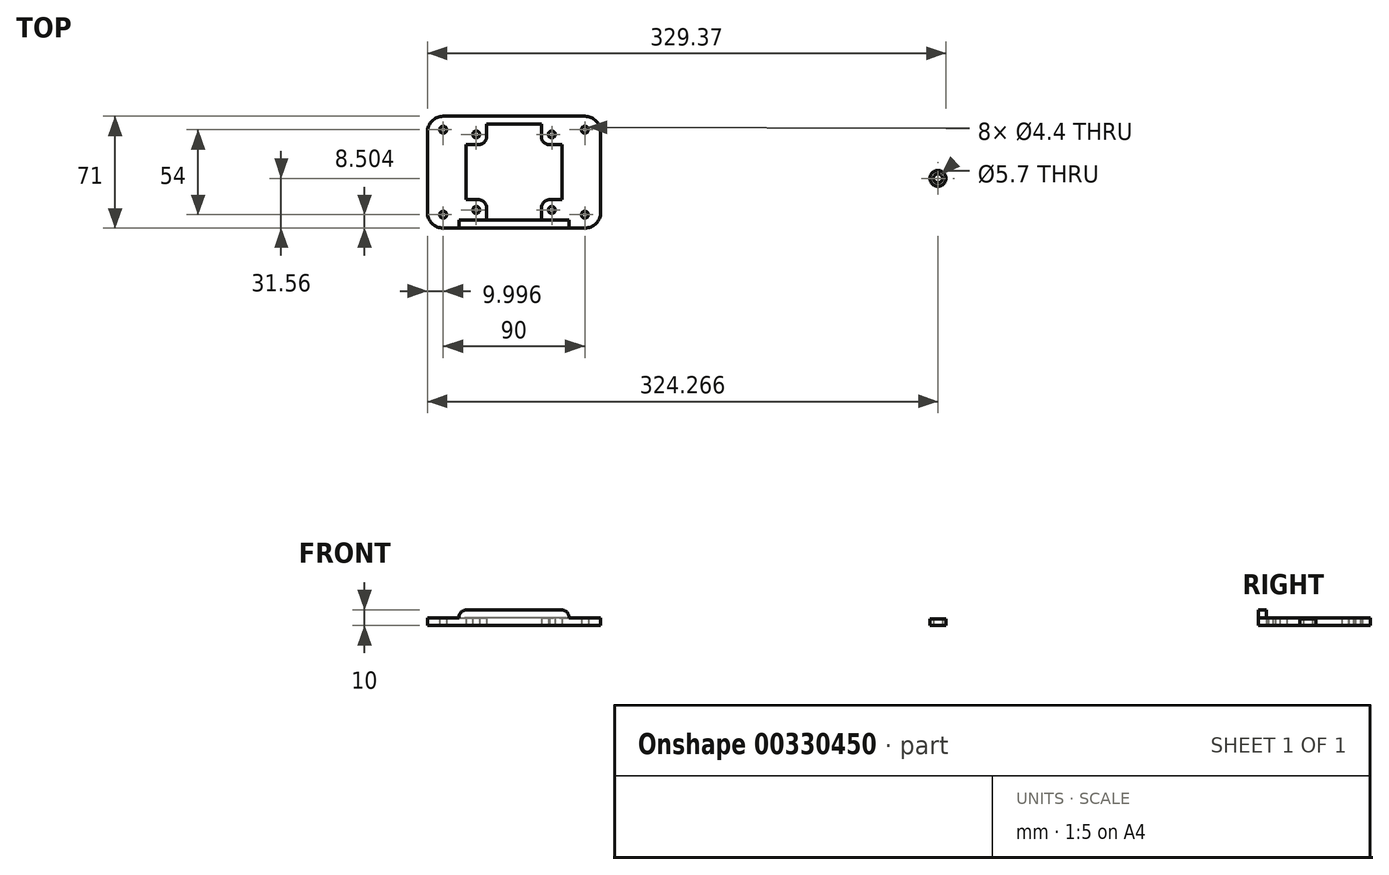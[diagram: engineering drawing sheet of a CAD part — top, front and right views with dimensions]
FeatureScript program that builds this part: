
annotation { "Feature Type Name" : "Feature", "Feature Type Description" : "" }
export const myFeature = defineFeature(function(context is Context, id is Id, definition is map)
    precondition{}
    {
        {
            var Q0;
            Q0=qCreatedBy(makeId("Top.planeOp"),FACE);
            var sketch = newSketch(context, id + "F0", { "sketchPlane" : qUnion([Q0])});
            skCircle(sketch, "E0", {"center": v(-176.65, -20.06) * mm, "radius": 2.2 * mm});
            skCircle(sketch, "E1.MirrorC", {"center": v(-128.65, -20.06) * mm, "radius": 2.2 * mm});
            skCircle(sketch, "E2.MirrorC", {"center": v(-176.65, 27.94) * mm, "radius": 2.2 * mm});
            skCircle(sketch, "E3.MirrorC", {"center": v(-128.65, 27.94) * mm, "radius": 2.2 * mm});
            skLineSegment(sketch, "E4.0", {"start": v(-183.15, -13.56) * mm, "end": v(-183.15, 21.44) * mm});
            skLineSegment(sketch, "E4.1", {"start": v(-183.15, -13.56) * mm, "end": v(-175.15, -13.56) * mm});
            skArc(sketch, "E4.2", {"start": v(-170.15, -18.56) * mm, "mid": v(-171.62, -15.02) * mm, "end": v(-175.15, -13.56) * mm});
            skLineSegment(sketch, "E4.3", {"start": v(-170.15, -26.56) * mm, "end": v(-170.15, -18.56) * mm});
            skLineSegment(sketch, "E4.4", {"start": v(-135.15, -26.56) * mm, "end": v(-170.15, -26.56) * mm});
            skLineSegment(sketch, "E4.5", {"start": v(-135.15, 34.44) * mm, "end": v(-135.15, 25.44) * mm});
            skLineSegment(sketch, "E4.6", {"start": v(-135.15, 34.44) * mm, "end": v(-170.15, 34.44) * mm});
            skLineSegment(sketch, "E4.7", {"start": v(-170.15, 34.44) * mm, "end": v(-170.15, 26.44) * mm});
            skArc(sketch, "E4.8", {"start": v(-170.15, 26.44) * mm, "mid": v(-171.62, 22.9) * mm, "end": v(-175.15, 21.44) * mm});
            skArc(sketch, "E4.9", {"start": v(-135.15, 25.44) * mm, "mid": v(-133.38, 22.54) * mm, "end": v(-130.15, 21.44) * mm});
            skLineSegment(sketch, "E4.10", {"start": v(-122.15, 21.44) * mm, "end": v(-130.15, 21.44) * mm});
            skLineSegment(sketch, "E4.11", {"start": v(-122.15, -13.56) * mm, "end": v(-122.15, 21.44) * mm});
            skLineSegment(sketch, "E4.12", {"start": v(-122.15, -13.56) * mm, "end": v(-130.15, -13.56) * mm});
            skArc(sketch, "E4.13", {"start": v(-135.15, -18.56) * mm, "mid": v(-133.69, -15.02) * mm, "end": v(-130.15, -13.56) * mm});
            skLineSegment(sketch, "E4.14", {"start": v(-183.15, 21.44) * mm, "end": v(-175.15, 21.44) * mm});
            skLineSegment(sketch, "E4.15", {"start": v(-135.15, -26.56) * mm, "end": v(-135.15, -18.56) * mm});
            skLineSegment(sketch, "E5", {"start": v(-183.15, -13.56) * mm, "end": v(-122.15, 21.44) * mm, "construction": true});
            skLineSegment(sketch, "E6", {"start": v(-152.65, 34.44) * mm, "end": v(-152.65, -26.56) * mm, "construction": true});
            skLineSegment(sketch, "E7", {"start": v(-152.65, -31.56) * mm, "end": v(-207.65, -31.56) * mm});
            skLineSegment(sketch, "E8", {"start": v(-207.65, -31.56) * mm, "end": v(-207.65, 39.44) * mm});
            skLineSegment(sketch, "E9", {"start": v(-207.65, 39.44) * mm, "end": v(-152.65, 39.44) * mm});
            skCircle(sketch, "E10", {"center": v(-197.65, 30.94) * mm, "radius": 2.2 * mm});
            skCircle(sketch, "E11", {"center": v(-197.65, -23.06) * mm, "radius": 2.2 * mm});
            skLineSegment(sketch, "E12", {"start": v(-183.15, 3.94) * mm, "end": v(-207.65, 3.94) * mm, "construction": true});
            skLineSegment(sketch, "E13.MirrorCS", {"start": v(-152.65, -31.56) * mm, "end": v(-97.65, -31.56) * mm});
            skLineSegment(sketch, "E14.MirrorCS", {"start": v(-97.65, 39.44) * mm, "end": v(-152.65, 39.44) * mm});
            skLineSegment(sketch, "E15.MirrorCS", {"start": v(-97.65, -31.56) * mm, "end": v(-97.65, 39.44) * mm});
            skCircle(sketch, "E16.MirrorC", {"center": v(-107.65, 30.94) * mm, "radius": 2.2 * mm});
            skCircle(sketch, "E17.MirrorC", {"center": v(-107.65, -23.06) * mm, "radius": 2.2 * mm});
            skSolve(sketch);
        }
        {
            var Q0;
            Q0=makeQuery(id+"F0.imprint","IMPRINT",FACE,{"disambiguationData":[TD([[makeQuery(id+"F0.imprint","IMPRINT",EDGE,{"derivedFrom":sQuery(id+"F0.wireOp",EDGE,"E0")}),-1.0]])]});
            extrude(context, id + "F1", {"entities" : qUnion([Q0]), "depth" : 5 * mm, "offsetDistance" : 25 * mm});
        }
        {
            var Q0;
            Q0=makeQuery(id+"F1.opExtrude","SWEPT_EDGE",EDGE,{"disambiguationData":[OSD([sQuery(id+"F0.wireOp",EDGE,"E7"),sQuery(id+"F0.wireOp",EDGE,"E8")])]});
            var Q1;
            Q1=makeQuery(id+"F1.opExtrude","SWEPT_EDGE",EDGE,{"disambiguationData":[OSD([sQuery(id+"F0.wireOp",EDGE,"E8"),sQuery(id+"F0.wireOp",EDGE,"E9")])]});
            var Q2;
            Q2=makeQuery(id+"F1.opExtrude","SWEPT_EDGE",EDGE,{"disambiguationData":[OSD([sQuery(id+"F0.wireOp",EDGE,"E13.MirrorCS"),sQuery(id+"F0.wireOp",EDGE,"E15.MirrorCS")])]});
            var Q3;
            Q3=makeQuery(id+"F1.opExtrude","SWEPT_EDGE",EDGE,{"disambiguationData":[OSD([sQuery(id+"F0.wireOp",EDGE,"E14.MirrorCS"),sQuery(id+"F0.wireOp",EDGE,"E15.MirrorCS")])]});
            fillet(context, id + "F2", {"entities" : qUnion([Q0, Q1, Q2, Q3]), "radius" : 10 * mm, "tangentPropagation" : true, "allowEdgeOverflow" : false});
        }
        {
            var Q0;
            Q0=makeQuery(id+"F1.opExtrude","CAP_FACE",FACE,{"disambiguationData":[OSD([sQuery(id+"F0.wireOp",EDGE,"E0"),sQuery(id+"F0.wireOp",EDGE,"E1.MirrorC"),sQuery(id+"F0.wireOp",EDGE,"E2.MirrorC"),sQuery(id+"F0.wireOp",EDGE,"E3.MirrorC"),sQuery(id+"F0.wireOp",EDGE,"E4.0"),sQuery(id+"F0.wireOp",EDGE,"E4.1"),sQuery(id+"F0.wireOp",EDGE,"E4.2"),sQuery(id+"F0.wireOp",EDGE,"E4.3"),sQuery(id+"F0.wireOp",EDGE,"E4.4"),sQuery(id+"F0.wireOp",EDGE,"E4.5"),sQuery(id+"F0.wireOp",EDGE,"E4.6"),sQuery(id+"F0.wireOp",EDGE,"E4.7"),sQuery(id+"F0.wireOp",EDGE,"E4.8"),sQuery(id+"F0.wireOp",EDGE,"E4.9"),sQuery(id+"F0.wireOp",EDGE,"E4.10"),sQuery(id+"F0.wireOp",EDGE,"E4.11"),sQuery(id+"F0.wireOp",EDGE,"E4.12"),sQuery(id+"F0.wireOp",EDGE,"E4.13"),sQuery(id+"F0.wireOp",EDGE,"E4.14"),sQuery(id+"F0.wireOp",EDGE,"E4.15"),sQuery(id+"F0.wireOp",EDGE,"E7"),sQuery(id+"F0.wireOp",EDGE,"E8"),sQuery(id+"F0.wireOp",EDGE,"E9"),sQuery(id+"F0.wireOp",EDGE,"E10"),sQuery(id+"F0.wireOp",EDGE,"E11"),sQuery(id+"F0.wireOp",EDGE,"E13.MirrorCS"),sQuery(id+"F0.wireOp",EDGE,"E14.MirrorCS"),sQuery(id+"F0.wireOp",EDGE,"E15.MirrorCS"),sQuery(id+"F0.wireOp",EDGE,"E16.MirrorC"),sQuery(id+"F0.wireOp",EDGE,"E17.MirrorC")])],"isStart":false});
            var sketch = newSketch(context, id + "F3", { "sketchPlane" : qUnion([Q0])});
            skLineSegment(sketch, "E18", {"start": v(-135.15, -26.56) * mm, "end": v(-117.65, -26.56) * mm});
            skLineSegment(sketch, "E19", {"start": v(-183.15, 3.94) * mm, "end": v(-197.76, 3.94) * mm, "construction": true});
            skLineSegment(sketch, "E20.MirrorCS", {"start": v(-170.15, 34.44) * mm, "end": v(-187.65, 34.44) * mm});
            skLineSegment(sketch, "E21.MirrorCS", {"start": v(-135.15, 34.44) * mm, "end": v(-117.65, 34.44) * mm});
            skLineSegment(sketch, "E22", {"start": v(-187.65, -26.56) * mm, "end": v(-187.65, -31.56) * mm});
            skLineSegment(sketch, "E23", {"start": v(-117.65, -26.56) * mm, "end": v(-117.65, -31.56) * mm});
            skPoint(sketch, "E24.start.orphan", {"position": v(-107.65, -31.56) * mm});
            skPoint(sketch, "E25.end.orphan", {"position": v(-197.65, -31.56) * mm});
            skPoint(sketch, "E26.orphan", {"position": v(-107.65, -26.56) * mm});
            skPoint(sketch, "E27.orphan", {"position": v(-197.65, -26.56) * mm});
            skPoint(sketch, "E28.start.orphan", {"position": v(-170.15, -26.56) * mm});
            skLineSegment(sketch, "E29", {"start": v(-187.65, -26.56) * mm, "end": v(-170.15, -26.56) * mm});
            skLineSegment(sketch, "E30.MirrorCS", {"start": v(-187.65, 34.44) * mm, "end": v(-170.15, 34.44) * mm});
            skLineSegment(sketch, "E31.MirrorCS", {"start": v(-187.65, 34.44) * mm, "end": v(-187.65, 39.44) * mm});
            skLineSegment(sketch, "E32.MirrorCS", {"start": v(-117.65, 34.44) * mm, "end": v(-117.65, 39.44) * mm});
            skPoint(sketch, "E33.orphan", {"position": v(-197.65, 34.44) * mm});
            skPoint(sketch, "E34.MirrorCS.end.orphan", {"position": v(-197.65, 39.44) * mm});
            skPoint(sketch, "E35.MirrorCS.end.orphan", {"position": v(-107.65, 34.44) * mm});
            skPoint(sketch, "E35.MirrorCS.start.orphan", {"position": v(-107.65, 39.44) * mm});
            skSolve(sketch);
        }
        {
            var Q0;
            Q0=makeQuery(id+"F3.imprint","IMPRINT",FACE,{"disambiguationData":[TD([[makeQuery(id+"F3.imprint","IMPRINT",EDGE,{"derivedFrom":sQuery(id+"F3.wireOp",EDGE,"E30.MirrorCS")}),1.0]])]});
            var Q1;
            Q1=makeQuery(id+"F3.imprint","IMPRINT",FACE,{"disambiguationData":[TD([[makeQuery(id+"F3.imprint","IMPRINT",EDGE,{"derivedFrom":sQuery(id+"F3.wireOp",EDGE,"E18")}),-1.0]])]});
            extrude(context, id + "F4", {"entities" : qUnion([Q0, Q1]), "operationType" : NewBodyOperationType.ADD, "depth" : 5 * mm, "offsetDistance" : 25 * mm});
        }
        {
            var Q0;
            Q0=makeQuery(id+"F4.opExtrude","CAP_EDGE",EDGE,{"disambiguationData":[OSD([sQuery(id+"F3.wireOp",EDGE,"E22")])],"isStart":false});
            var Q1;
            Q1=makeQuery(id+"F4.opExtrude","CAP_EDGE",EDGE,{"disambiguationData":[OSD([sQuery(id+"F3.wireOp",EDGE,"E23")])],"isStart":false});
            var Q2;
            Q2=makeQuery(id+"F4.opExtrude","CAP_EDGE",EDGE,{"disambiguationData":[OSD([sQuery(id+"F3.wireOp",EDGE,"E32.MirrorCS")])],"isStart":false});
            var Q3;
            Q3=makeQuery(id+"F4.opExtrude","CAP_EDGE",EDGE,{"disambiguationData":[OSD([sQuery(id+"F3.wireOp",EDGE,"E31.MirrorCS")])],"isStart":false});
            fillet(context, id + "F5", {"entities" : qUnion([Q0, Q1, Q2, Q3]), "radius" : 5 * mm, "tangentPropagation" : true, "allowEdgeOverflow" : false});
        }
        {
            var Q0;
            Q0=qCreatedBy(makeId("Top.planeOp"),FACE);
            var sketch = newSketch(context, id + "F6", { "sketchPlane" : qUnion([Q0])});
            skCircle(sketch, "E36", {"center": v(116.62, 0) * mm, "radius": 2.85 * mm});
            skCircle(sketch, "E37", {"center": v(116.62, 0) * mm, "radius": 5.1 * mm});
            skSolve(sketch);
        }
        {
            var Q0;
            Q0=makeQuery(id+"F6.imprint","IMPRINT",FACE,{"disambiguationData":[TD([[makeQuery(id+"F6.imprint","IMPRINT",EDGE,{"derivedFrom":sQuery(id+"F6.wireOp",EDGE,"E36")}),-1.0]])]});
            extrude(context, id + "F7", {"entities" : qUnion([Q0]), "depth" : 4.4 * mm, "offsetDistance" : 25 * mm});
        }
    });
